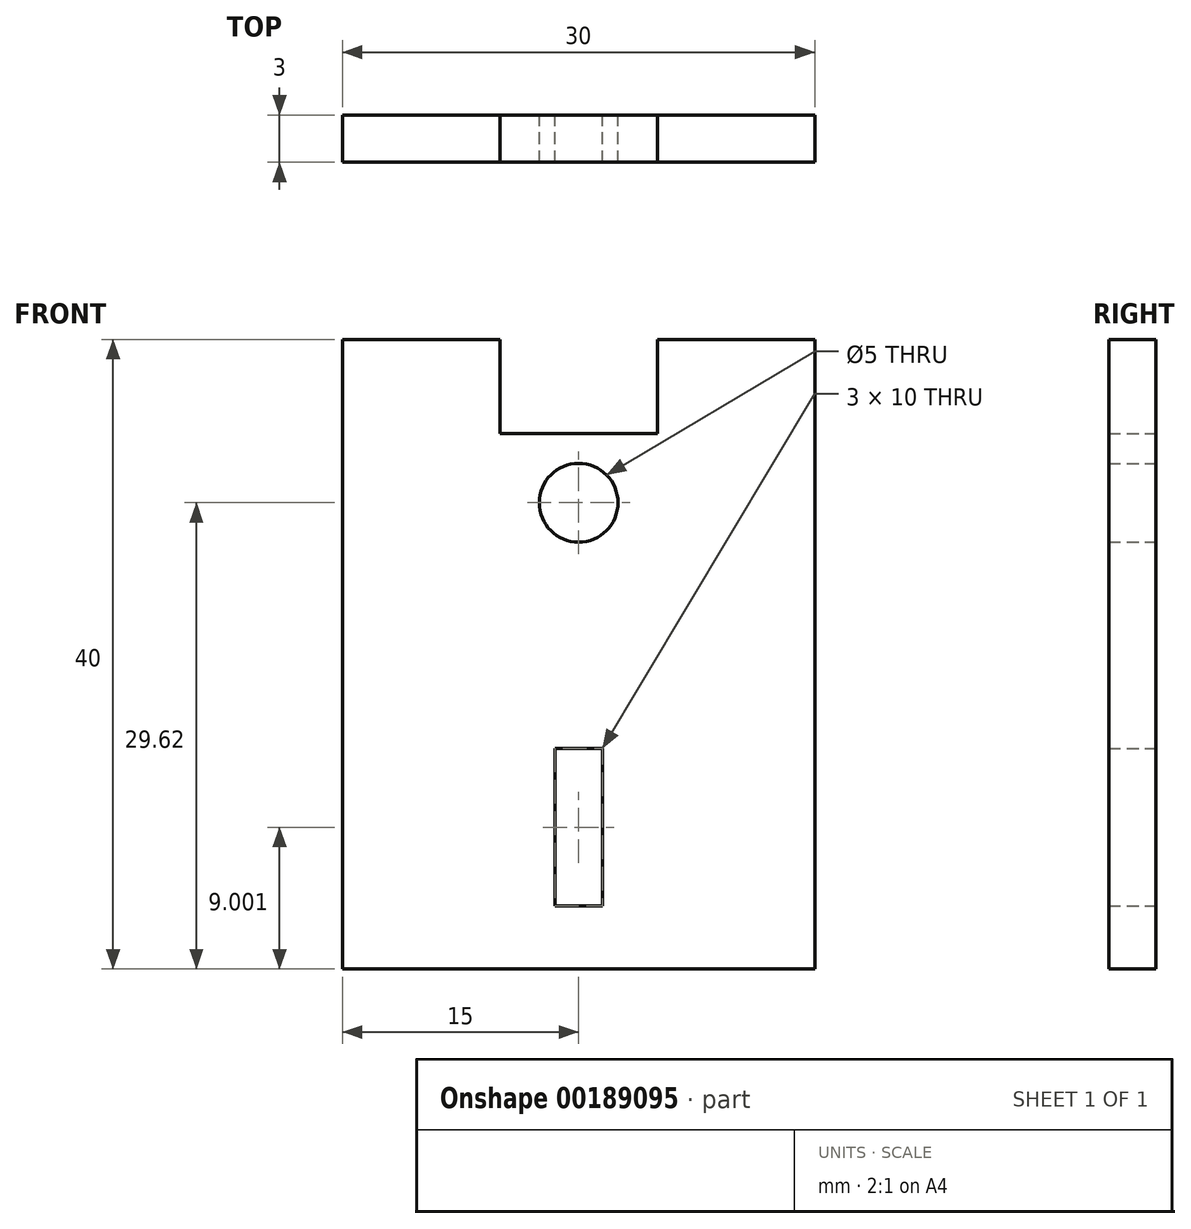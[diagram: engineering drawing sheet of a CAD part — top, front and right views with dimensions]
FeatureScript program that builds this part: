
annotation { "Feature Type Name" : "Feature", "Feature Type Description" : "" }
export const myFeature = defineFeature(function(context is Context, id is Id, definition is map)
    precondition{}
    {
        {
            var Q0;
            Q0=qCreatedBy(makeId("Front.planeOp"),FACE);
            var sketch = newSketch(context, id + "F0", { "sketchPlane" : qUnion([Q0])});
            skLineSegment(sketch, "E0.bottom", {"start": v(-5, 4.38) * mm, "end": v(5, 4.38) * mm});
            skPoint(sketch, "E0.middle", {"position": v(0, 0) * mm});
            skLineSegment(sketch, "E1.top", {"start": v(-15, 10.38) * mm, "end": v(-5, 10.38) * mm});
            skLineSegment(sketch, "E1.right", {"start": v(-5, 4.38) * mm, "end": v(-5, 10.38) * mm});
            skLineSegment(sketch, "E2.top", {"start": v(15, 10.38) * mm, "end": v(5, 10.38) * mm});
            skLineSegment(sketch, "E2.right", {"start": v(5, 4.38) * mm, "end": v(5, 10.38) * mm});
            skCircle(sketch, "E3", {"center": v(0, 0) * mm, "radius": 2.5 * mm});
            skLineSegment(sketch, "E4", {"start": v(-15, -29.62) * mm, "end": v(15, -29.62) * mm});
            skLineSegment(sketch, "E5.bottom", {"start": v(1.5, -15.62) * mm, "end": v(-1.5, -15.62) * mm});
            skLineSegment(sketch, "E5.top", {"start": v(1.5, -25.62) * mm, "end": v(-1.5, -25.62) * mm});
            skLineSegment(sketch, "E5.left", {"start": v(1.5, -15.62) * mm, "end": v(1.5, -25.62) * mm});
            skLineSegment(sketch, "E5.right", {"start": v(-1.5, -15.62) * mm, "end": v(-1.5, -25.62) * mm});
            skPoint(sketch, "E5.middle", {"position": v(0, -20.62) * mm});
            skLineSegment(sketch, "E6", {"start": v(-15, 10.38) * mm, "end": v(-15, -29.62) * mm});
            skLineSegment(sketch, "E7", {"start": v(15, -29.62) * mm, "end": v(15, 10.38) * mm});
            skSolve(sketch);
        }
        {
            var Q0;
            Q0=makeQuery(id+"F0.imprint","IMPRINT",FACE,{"disambiguationData":[TD([[makeQuery(id+"F0.imprint","IMPRINT",EDGE,{"derivedFrom":sQuery(id+"F0.wireOp",EDGE,"E0.bottom")}),-1.0]])]});
            extrude(context, id + "F1", {"entities" : qUnion([Q0]), "depth" : 3 * mm});
        }
    });
